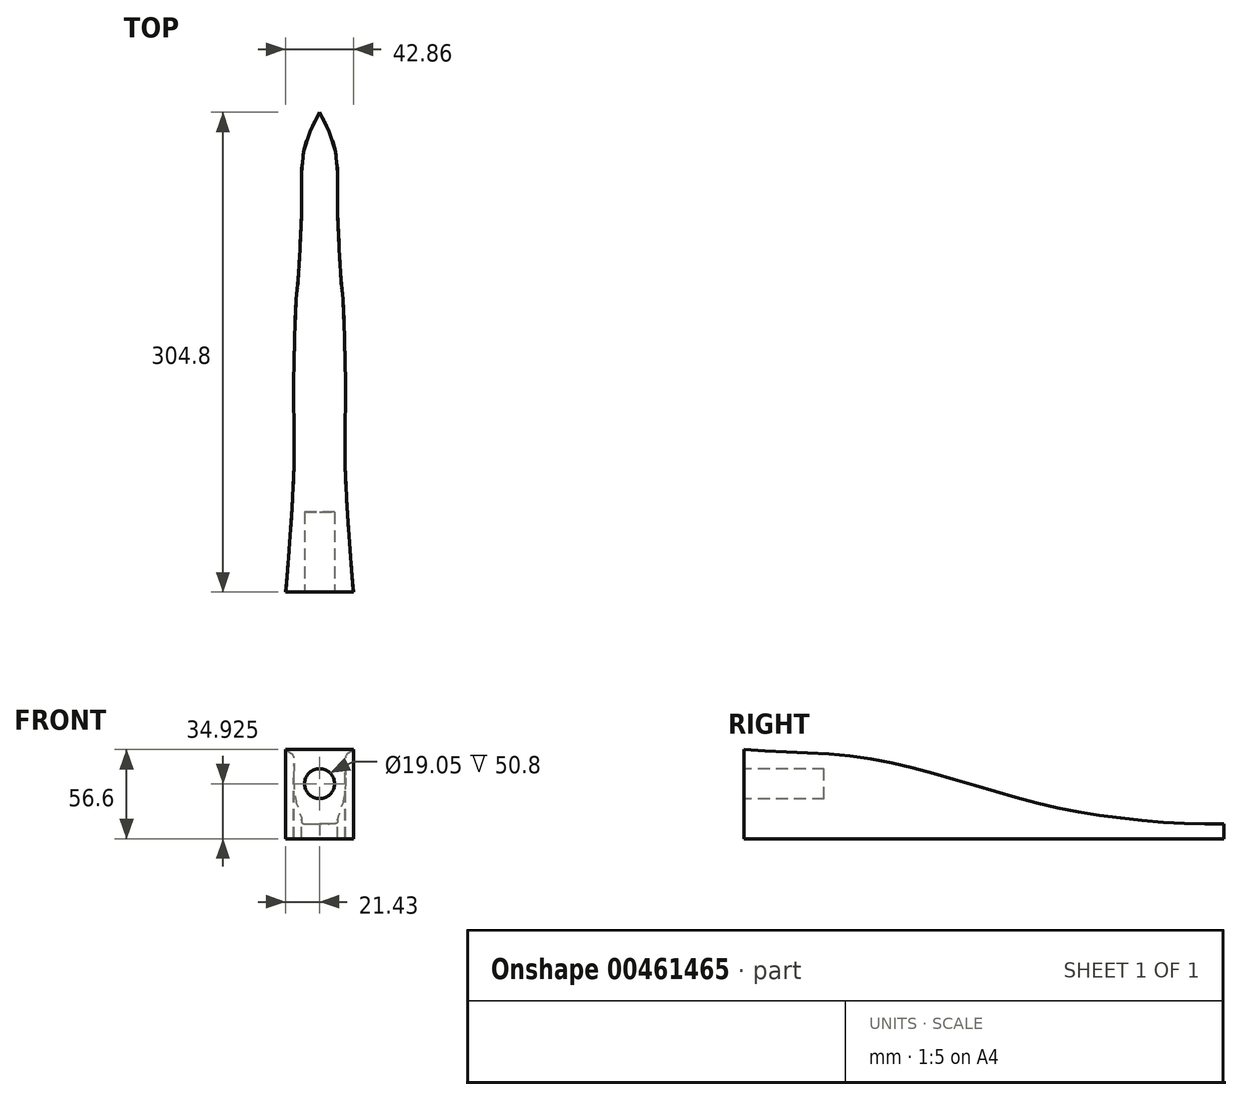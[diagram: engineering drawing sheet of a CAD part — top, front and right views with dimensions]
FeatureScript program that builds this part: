
annotation { "Feature Type Name" : "Feature", "Feature Type Description" : "" }
export const myFeature = defineFeature(function(context is Context, id is Id, definition is map)
    precondition{}
    {
        {
            var Q0;
            Q0=qCreatedBy(makeId("Right.planeOp"),FACE);
            var sketch = newSketch(context, id + "F0", { "sketchPlane" : qUnion([Q0])});
            skLineSegment(sketch, "E0", {"start": v(-152.4, 0) * mm, "end": v(152.4, 0) * mm});
            skLineSegment(sketch, "E1", {"start": v(-152.4, 0) * mm, "end": v(-152.4, 69.85) * mm});
            skLineSegment(sketch, "E2", {"start": v(152.4, 0) * mm, "end": v(152.4, 19.05) * mm});
            skLineSegment(sketch, "E3", {"start": v(152.4, 19.05) * mm, "end": v(-152.4, 69.85) * mm});
            skPoint(sketch, "E4.endSnap0", {"position": v(-152.4, 34.93) * mm});
            skLineSegment(sketch, "E5.0", {"start": v(-95.25, 50.8) * mm, "end": v(-152.4, 50.8) * mm, "construction": true});
            skLineSegment(sketch, "E5.1", {"start": v(-95.25, 50.8) * mm, "end": v(-95.25, 19.05) * mm, "construction": true});
            skLineSegment(sketch, "E5.2", {"start": v(-95.25, 19.05) * mm, "end": v(-152.4, 19.05) * mm, "construction": true});
            skSolve(sketch);
        }
        {
            var Q0;
            Q0=makeQuery(id+"F0.imprint","IMPRINT",FACE,{"disambiguationData":[TD([[makeQuery(id+"F0.imprint","IMPRINT",EDGE,{"derivedFrom":sQuery(id+"F0.wireOp",EDGE,"E0")}),1.0]])]});
            extrude(context, id + "F1", {"entities" : qUnion([Q0]), "depth" : 42.86 * mm, "symmetric" : true});
        }
        {
            var Q0;
            Q0=makeQuery(id+"F1.opExtrude","SWEPT_FACE",FACE,{"disambiguationData":[OSD([sQuery(id+"F0.wireOp",EDGE,"E1")])]});
            var sketch = newSketch(context, id + "F2", { "sketchPlane" : qUnion([Q0])});
            skLineSegment(sketch, "E6", {"start": v(21.43, 34.93) * mm, "end": v(0, 34.93) * mm, "construction": true});
            skCircle(sketch, "E7", {"center": v(0, 34.93) * mm, "radius": 9.53 * mm});
            skSolve(sketch);
        }
        {
            var Q0;
            Q0=makeQuery(id+"F2.imprint","IMPRINT",FACE,{"disambiguationData":[TD([[makeQuery(id+"F2.imprint","IMPRINT",EDGE,{"derivedFrom":sQuery(id+"F2.wireOp",EDGE,"E7")}),1.0]])]});
            var Q1;
            Q1=sQuery(id+"F2.wireOp",EDGE,"E7");
            extrude(context, id + "F3", {"entities" : qUnion([Q0]), "operationType" : NewBodyOperationType.REMOVE, "surfaceEntities" : qUnion([Q1]), "oppositeDirection" : true, "depth" : 50.8 * mm});
        }
        {
            var Q0;
            Q0=makeQuery(id+"F1.opExtrude","CAP_FACE",FACE,{"disambiguationData":[OSD([sQuery(id+"F0.wireOp",EDGE,"E0"),sQuery(id+"F0.wireOp",EDGE,"E1"),sQuery(id+"F0.wireOp",EDGE,"E2"),sQuery(id+"F0.wireOp",EDGE,"E3")])],"isStart":false});
            var sketch = newSketch(context, id + "F4", { "sketchPlane" : qUnion([Q0])});
            skLineSegment(sketch, "E8", {"start": v(-152.4, 34.93) * mm, "end": v(-152.4, 44.45) * mm, "construction": true});
            skLineSegment(sketch, "E9.0", {"start": v(-95.25, 19.05) * mm, "end": v(-152.4, 19.05) * mm, "construction": true});
            skLineSegment(sketch, "E9.1", {"start": v(-95.25, 50.8) * mm, "end": v(-95.25, 19.05) * mm, "construction": true});
            skLineSegment(sketch, "E9.2", {"start": v(-152.4, 50.8) * mm, "end": v(-95.25, 50.8) * mm, "construction": true});
            skLineSegment(sketch, "E10", {"start": v(57.15, 0) * mm, "end": v(57.15, 34.93) * mm, "construction": true});
            skLineSegment(sketch, "E11", {"start": v(-152.4, 44.45) * mm, "end": v(-101.6, 44.45) * mm, "construction": true});
            skLineSegment(sketch, "E12", {"start": v(-101.6, 44.45) * mm, "end": v(-101.6, 25.4) * mm, "construction": true});
            skLineSegment(sketch, "E13", {"start": v(-101.6, 25.4) * mm, "end": v(-152.4, 25.4) * mm, "construction": true});
            skPoint(sketch, "E14.1.internal.snap0", {"position": v(152.4, 9.53) * mm});
            skFitSpline(sketch, "E14", {"points": [v(152.4, 9.53) * mm, v(128.35, 9.53) * mm, v(57.15, 17.46) * mm, v(0, 32.07) * mm, v(-80.15, 51.86) * mm, v(-152.4, 56.6) * mm], "startDerivative": vector(-159.27, -5.24) * mm, "endDerivative": vector(-320.51, 31.47) * mm});
            skSolve(sketch);
        }
        {
            var Q0;
            Q0=makeQuery(id+"F1.opExtrude","SWEPT_FACE",FACE,{"disambiguationData":[OSD([sQuery(id+"F0.wireOp",EDGE,"E0")])]});
            var sketch = newSketch(context, id + "F5", { "sketchPlane" : qUnion([Q0])});
            skLineSegment(sketch, "E15", {"start": v(0, 152.4) * mm, "end": v(0, -152.4) * mm, "construction": true});
            skLineSegment(sketch, "E16", {"start": v(21.43, -57.15) * mm, "end": v(-21.43, -57.15) * mm, "construction": true});
            skLineSegment(sketch, "E17", {"start": v(15.88, 152.4) * mm, "end": v(15.88, 95.25) * mm, "construction": true});
            skLineSegment(sketch, "E18", {"start": v(15.88, 95.25) * mm, "end": v(-15.87, 95.25) * mm, "construction": true});
            skLineSegment(sketch, "E19", {"start": v(-15.87, 95.25) * mm, "end": v(-15.87, 152.4) * mm, "construction": true});
            skLineSegment(sketch, "E20", {"start": v(0, 152.4) * mm, "end": v(-9.53, 152.4) * mm, "construction": true});
            skLineSegment(sketch, "E21", {"start": v(-9.53, 152.4) * mm, "end": v(-9.53, 101.6) * mm, "construction": true});
            skLineSegment(sketch, "E22", {"start": v(-9.52, 101.6) * mm, "end": v(9.53, 101.6) * mm, "construction": true});
            skLineSegment(sketch, "E23", {"start": v(9.53, 101.6) * mm, "end": v(9.53, 152.4) * mm, "construction": true});
            skFitSpline(sketch, "E24", {"points": [v(0, -152.4) * mm, v(8.69, -133.34) * mm, v(11.4, -114.35) * mm, v(11.4, -92.3) * mm, v(12.42, -68.22) * mm, v(13.78, -43.12) * mm, v(14.45, -37.7) * mm, v(16.15, 0) * mm, v(16.49, 29.8) * mm, v(16.15, 69.15) * mm, v(21.43, 152.4) * mm], "startDerivative": vector(116.42, 219.37) * mm, "endDerivative": vector(41.43, 523.05) * mm});
            skFitSpline(sketch, "E25.MirrorCS", {"points": [v(0, -152.4) * mm, v(-8.69, -133.34) * mm, v(-11.4, -114.35) * mm, v(-11.4, -92.3) * mm, v(-12.42, -68.22) * mm, v(-13.78, -43.12) * mm, v(-14.45, -37.7) * mm, v(-16.15, 0) * mm, v(-16.49, 29.8) * mm, v(-16.15, 69.15) * mm, v(-21.43, 152.4) * mm], "startDerivative": vector(-116.42, 219.37) * mm, "endDerivative": vector(-41.43, 523.05) * mm});
            skSolve(sketch);
        }
        {
            var Q0;
            {var subQ0=sQuery(id+"F4.wireOp",EDGE,"E14");Q0=makeQuery(id+"F4.imprint","IMPRINT",FACE,{"disambiguationData":[TD([[makeQuery(id+"F4.imprint","IMPRINT",EDGE,{"derivedFrom":subQ0}),-1.0]])]});}
            extrude(context, id + "F6", {"entities" : qUnion([Q0]), "operationType" : NewBodyOperationType.REMOVE, "endBound" : BoundingType.UP_TO_NEXT, "oppositeDirection" : true, "depth" : 25.4 * mm, "offsetDistance" : 25.4 * mm});
        }
        {
            var Q0;
            Q0 = qSketchRegion(id + "F5", true);
            var Q1;
            {var subQ0=sQuery(id+"F5.wireOp",EDGE,"E25.MirrorCS");Q1=makeQuery(id+"F5.imprint","IMPRINT",FACE,{"disambiguationData":[TD([[makeQuery(id+"F5.imprint","IMPRINT",EDGE,{"derivedFrom":subQ0}),1.0]])]});}
            var Q2;
            {var subQ0=sQuery(id+"F5.wireOp",EDGE,"E24");Q2=makeQuery(id+"F5.imprint","IMPRINT",FACE,{"disambiguationData":[TD([[makeQuery(id+"F5.imprint","IMPRINT",EDGE,{"derivedFrom":subQ0}),-1.0]])]});}
            extrude(context, id + "F7", {"entities" : qUnion([Q0, Q1, Q2]), "operationType" : NewBodyOperationType.REMOVE, "endBound" : BoundingType.THROUGH_ALL, "oppositeDirection" : true, "depth" : 25.4 * mm, "offsetDistance" : 25.4 * mm});
        }
    });
